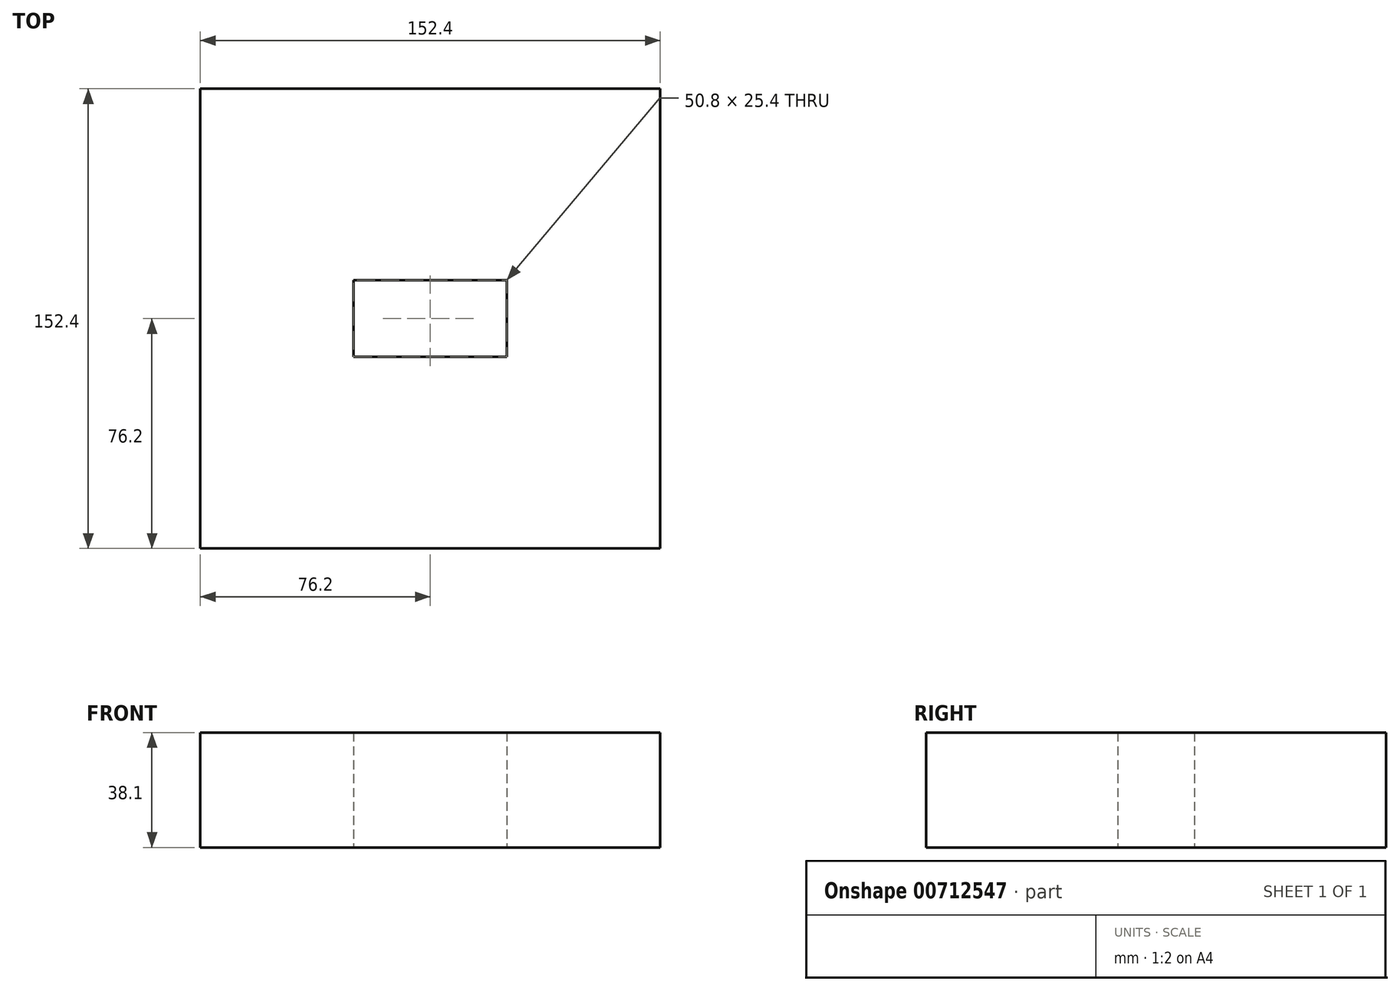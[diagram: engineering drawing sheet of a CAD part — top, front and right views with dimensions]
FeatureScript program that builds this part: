
annotation { "Feature Type Name" : "Feature", "Feature Type Description" : "" }
export const myFeature = defineFeature(function(context is Context, id is Id, definition is map)
    precondition{}
    {
        {
            var Q0;
            Q0=qCreatedBy(makeId("Top.planeOp"),FACE);
            var sketch = newSketch(context, id + "F0", { "sketchPlane" : qUnion([Q0])});
            skLineSegment(sketch, "E0.bottom", {"start": v(76.2, -76.2) * mm, "end": v(-76.2, -76.2) * mm});
            skLineSegment(sketch, "E0.top", {"start": v(76.2, 76.2) * mm, "end": v(-76.2, 76.2) * mm});
            skLineSegment(sketch, "E0.left", {"start": v(76.2, -76.2) * mm, "end": v(76.2, 76.2) * mm});
            skLineSegment(sketch, "E0.right", {"start": v(-76.2, -76.2) * mm, "end": v(-76.2, 76.2) * mm});
            skPoint(sketch, "E0.middle", {"position": v(0, 0) * mm});
            skLineSegment(sketch, "E1.bottom", {"start": v(25.4, -12.7) * mm, "end": v(-25.4, -12.7) * mm});
            skLineSegment(sketch, "E1.top", {"start": v(25.4, 12.7) * mm, "end": v(-25.4, 12.7) * mm});
            skLineSegment(sketch, "E1.left", {"start": v(25.4, -12.7) * mm, "end": v(25.4, 12.7) * mm});
            skLineSegment(sketch, "E1.right", {"start": v(-25.4, -12.7) * mm, "end": v(-25.4, 12.7) * mm});
            skSolve(sketch);
        }
        {
            var Q0;
            Q0=makeQuery(id+"F0.imprint","IMPRINT",FACE,{"disambiguationData":[TD([[makeQuery(id+"F0.imprint","IMPRINT",EDGE,{"derivedFrom":sQuery(id+"F0.wireOp",EDGE,"E0.bottom")}),-1.0]])]});
            extrude(context, id + "F1", {"entities" : qUnion([Q0]), "depth" : 38.1 * mm, "offsetDistance" : 25.4 * mm});
        }
    });
